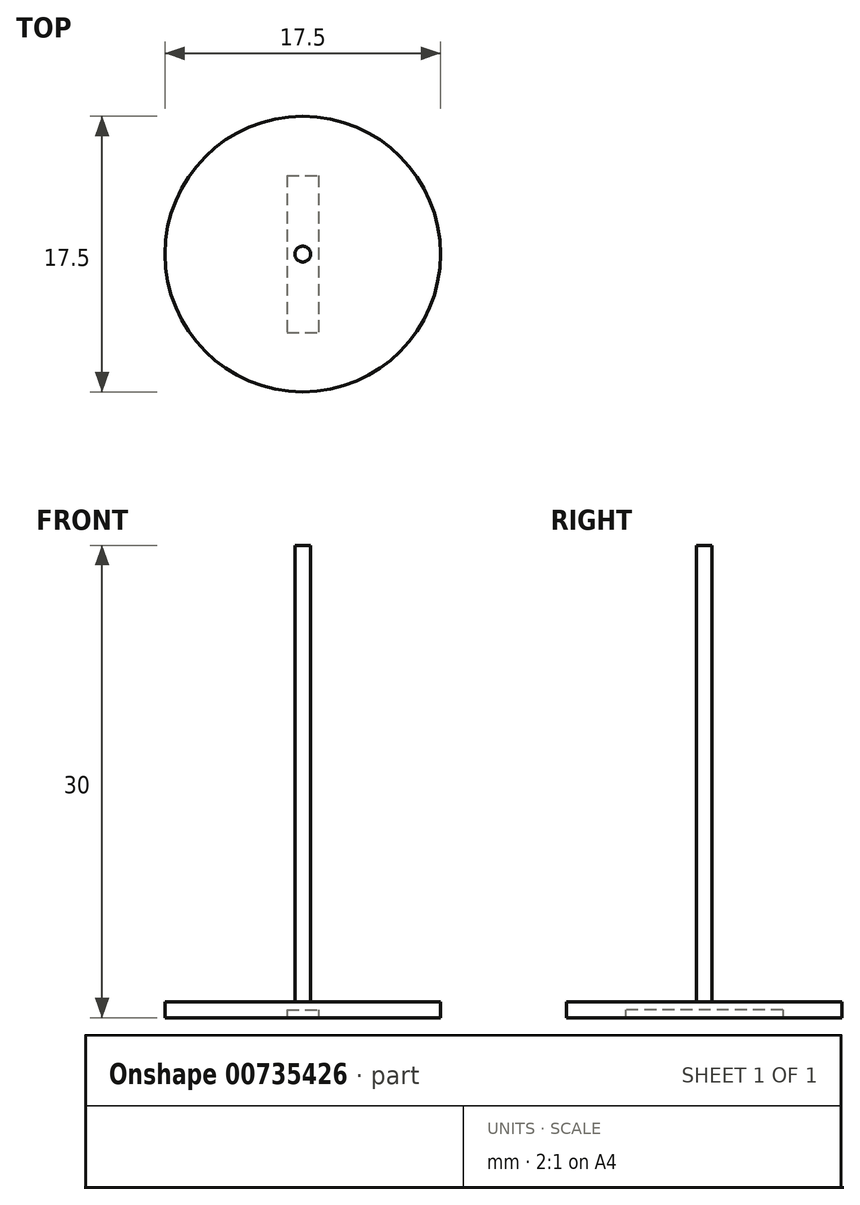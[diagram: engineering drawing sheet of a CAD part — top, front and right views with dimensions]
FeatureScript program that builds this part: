
annotation { "Feature Type Name" : "Feature", "Feature Type Description" : "" }
export const myFeature = defineFeature(function(context is Context, id is Id, definition is map)
    precondition{}
    {
        {
            var Q0;
            Q0=qCreatedBy(makeId("Top.planeOp"),FACE);
            var sketch = newSketch(context, id + "F0", { "sketchPlane" : qUnion([Q0])});
            skLineSegment(sketch, "E0.bottom", {"start": v(-7.82, 10.5) * mm, "end": v(9.68, 10.5) * mm});
            skLineSegment(sketch, "E0.top", {"start": v(-7.82, -7) * mm, "end": v(9.68, -7) * mm});
            skLineSegment(sketch, "E0.left", {"start": v(-7.82, 10.5) * mm, "end": v(-7.82, -7) * mm});
            skLineSegment(sketch, "E0.right", {"start": v(9.68, 10.5) * mm, "end": v(9.68, -7) * mm});
            skPoint(sketch, "E1.endSnap0", {"position": v(9.68, 1.75) * mm});
            skLineSegment(sketch, "E2", {"start": v(9.68, 1.75) * mm, "end": v(0.93, 1.75) * mm});
            skPoint(sketch, "E2.endSnap0", {"position": v(0.93, 10.5) * mm});
            skCircle(sketch, "E3", {"center": v(0.93, 1.75) * mm, "radius": 8.75 * mm});
            skCircle(sketch, "E4", {"center": v(0.93, 1.75) * mm, "radius": 8.25 * mm});
            skCircle(sketch, "E5", {"center": v(0.93, 1.75) * mm, "radius": 0.5 * mm});
            skSolve(sketch);
        }
        {
            var Q0;
            Q0=makeQuery(id+"F0.imprint","IMPRINT",FACE,{"disambiguationData":[TD([[makeQuery(id+"F0.imprint","IMPRINT",EDGE,{"derivedFrom":sQuery(id+"F0.wireOp",EDGE,"E5")}),1.0]])]});
            var Q1;
            Q1=makeQuery(id+"F0.imprint","IMPRINT",FACE,{"disambiguationData":[TD([[makeQuery(id+"F0.imprint","IMPRINT",EDGE,{"derivedFrom":sQuery(id+"F0.wireOp",EDGE,"E4")}),1.0]])]});
            var Q2;
            Q2=makeQuery(id+"F0.imprint","IMPRINT",FACE,{"disambiguationData":[TD([[makeQuery(id+"F0.imprint","IMPRINT",EDGE,{"derivedFrom":sQuery(id+"F0.wireOp",EDGE,"E4")}),-1.0]])]});
            extrude(context, id + "F1", {"entities" : qUnion([Q0, Q1, Q2]), "oppositeDirection" : true, "depth" : 1 * mm, "offsetDistance" : 25 * mm});
        }
        {
            var Q0;
            Q0=makeQuery(id+"F0.imprint","IMPRINT",FACE,{"disambiguationData":[TD([[makeQuery(id+"F0.imprint","IMPRINT",EDGE,{"derivedFrom":sQuery(id+"F0.wireOp",EDGE,"E5")}),1.0]])]});
            extrude(context, id + "F2", {"entities" : qUnion([Q0]), "depth" : 29 * mm, "offsetDistance" : 25 * mm});
        }
        {
            var Q0;
            Q0=makeQuery(id+"F1.opExtrude","CAP_FACE",FACE,{"disambiguationData":[OSD([sQuery(id+"F0.wireOp",EDGE,"E3")])],"isStart":false});
            var sketch = newSketch(context, id + "F3", { "sketchPlane" : qUnion([Q0])});
            skLineSegment(sketch, "E6.left", {"start": v(1.93, -6.75) * mm, "end": v(1.93, 3.25) * mm});
            skLineSegment(sketch, "E6.right", {"start": v(-0.07, -6.75) * mm, "end": v(-0.07, 3.25) * mm});
            skLineSegment(sketch, "E7", {"start": v(-0.07, -6.75) * mm, "end": v(1.93, -6.75) * mm});
            skLineSegment(sketch, "E8", {"start": v(-0.07, 3.25) * mm, "end": v(1.93, 3.25) * mm});
            skSolve(sketch);
        }
        {
            var Q0;
            Q0=makeQuery(id+"F3.imprint","IMPRINT",FACE,{"disambiguationData":[TD([[makeQuery(id+"F3.imprint","IMPRINT",EDGE,{"derivedFrom":sQuery(id+"F3.wireOp",EDGE,"E6.left")}),1.0]])]});
            extrude(context, id + "F4", {"entities" : qUnion([Q0]), "operationType" : NewBodyOperationType.REMOVE, "oppositeDirection" : true, "depth" : 0.5 * mm, "offsetDistance" : 25 * mm});
        }
    });
